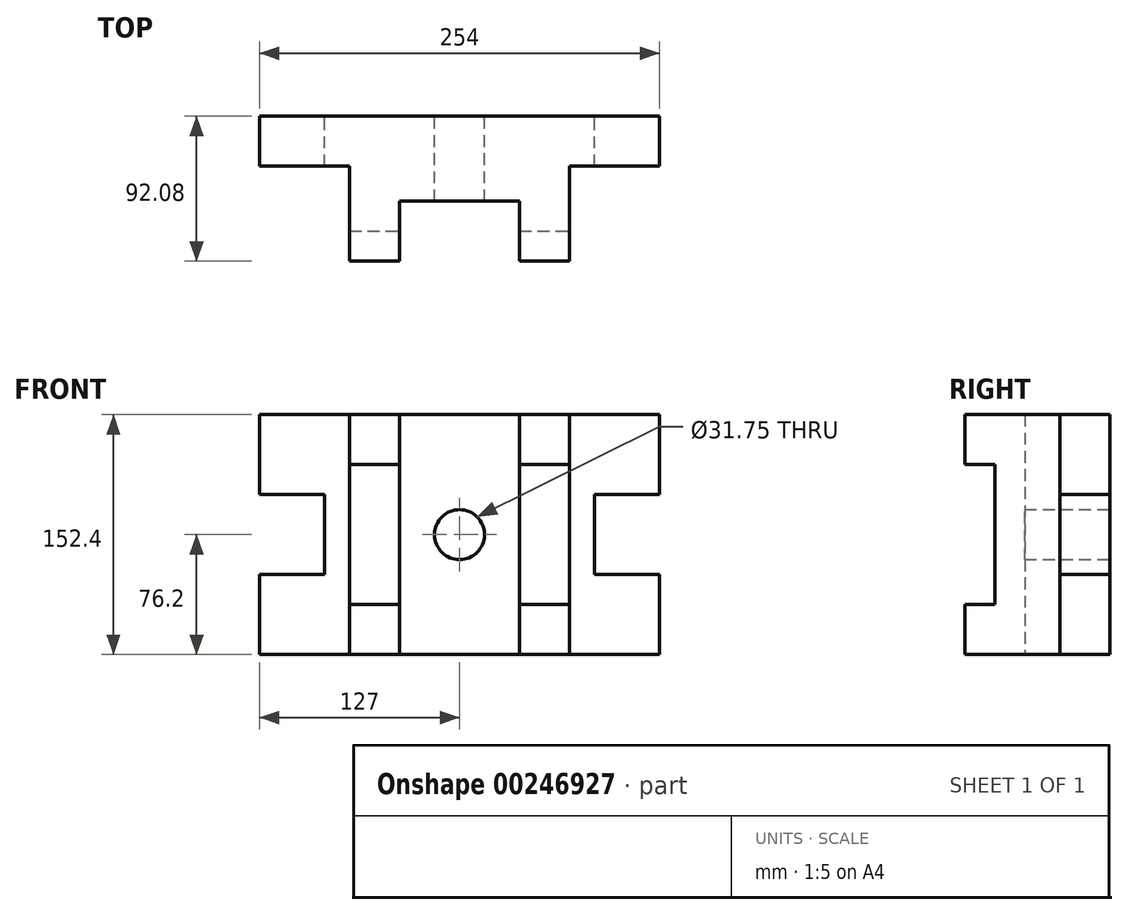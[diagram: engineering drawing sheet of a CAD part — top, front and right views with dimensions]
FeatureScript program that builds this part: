
annotation { "Feature Type Name" : "Feature", "Feature Type Description" : "" }
export const myFeature = defineFeature(function(context is Context, id is Id, definition is map)
    precondition{}
    {
        {
            var Q0;
            Q0=qCreatedBy(makeId("Front.planeOp"),FACE);
            var sketch = newSketch(context, id + "F0", { "sketchPlane" : qUnion([Q0])});
            skCircle(sketch, "E0", {"center": v(0, 0) * mm, "radius": 15.88 * mm});
            skLineSegment(sketch, "E1.bottom", {"start": v(-38.1, 76.2) * mm, "end": v(38.1, 76.2) * mm});
            skLineSegment(sketch, "E1.top", {"start": v(-38.1, -76.2) * mm, "end": v(38.1, -76.2) * mm});
            skLineSegment(sketch, "E1.left", {"start": v(-38.1, 76.2) * mm, "end": v(-38.1, -76.2) * mm});
            skLineSegment(sketch, "E1.right", {"start": v(38.1, 76.2) * mm, "end": v(38.1, -76.2) * mm});
            skLineSegment(sketch, "E2.bottom", {"start": v(-69.85, 76.2) * mm, "end": v(-38.1, 76.2) * mm});
            skLineSegment(sketch, "E2.top", {"start": v(-69.85, -76.2) * mm, "end": v(-38.1, -76.2) * mm});
            skLineSegment(sketch, "E2.left", {"start": v(-69.85, 76.2) * mm, "end": v(-69.85, -76.2) * mm});
            skPoint(sketch, "E2.middle", {"position": v(-53.97, 0) * mm});
            skLineSegment(sketch, "E3.top", {"start": v(98.71, -76.2) * mm, "end": v(130.46, -76.2) * mm});
            skLineSegment(sketch, "E4.bottom", {"start": v(69.85, 76.2) * mm, "end": v(127, 76.2) * mm});
            skLineSegment(sketch, "E4.top", {"start": v(69.85, -76.2) * mm, "end": v(127, -76.2) * mm});
            skLineSegment(sketch, "E4.left", {"start": v(69.85, 76.2) * mm, "end": v(69.85, -76.2) * mm});
            skLineSegment(sketch, "E4.right", {"start": v(127, 76.2) * mm, "end": v(127, -76.2) * mm});
            skPoint(sketch, "E4.middle", {"position": v(98.42, 0) * mm});
            skLineSegment(sketch, "E5.bottom", {"start": v(-69.85, 76.2) * mm, "end": v(-127, 76.2) * mm});
            skLineSegment(sketch, "E5.top", {"start": v(-69.85, -76.2) * mm, "end": v(-127, -76.2) * mm});
            skLineSegment(sketch, "E5.right", {"start": v(-127, 76.2) * mm, "end": v(-127, -76.2) * mm});
            skPoint(sketch, "E5.middle", {"position": v(-98.43, 0) * mm});
            skLineSegment(sketch, "E6", {"start": v(-69.85, 44.45) * mm, "end": v(-38.1, 44.45) * mm});
            skLineSegment(sketch, "E7", {"start": v(-69.85, -44.45) * mm, "end": v(-38.1, -44.45) * mm});
            skLineSegment(sketch, "E8.bottom", {"start": v(38.1, 76.2) * mm, "end": v(69.85, 76.2) * mm});
            skLineSegment(sketch, "E8.top", {"start": v(38.1, -76.2) * mm, "end": v(69.85, -76.2) * mm});
            skPoint(sketch, "E8.middle", {"position": v(53.98, 0) * mm});
            skLineSegment(sketch, "E9", {"start": v(38.1, 44.45) * mm, "end": v(69.85, 44.45) * mm});
            skLineSegment(sketch, "E10", {"start": v(38.1, -44.45) * mm, "end": v(69.85, -44.45) * mm});
            skLineSegment(sketch, "E11", {"start": v(-127, 25.4) * mm, "end": v(-85.72, 25.4) * mm});
            skLineSegment(sketch, "E12", {"start": v(-85.72, 25.4) * mm, "end": v(-85.72, -25.4) * mm});
            skLineSegment(sketch, "E13", {"start": v(-85.72, -25.4) * mm, "end": v(-127, -25.4) * mm});
            skLineSegment(sketch, "E14", {"start": v(127, 25.4) * mm, "end": v(85.72, 25.4) * mm});
            skLineSegment(sketch, "E15", {"start": v(85.72, 25.4) * mm, "end": v(85.72, -25.4) * mm});
            skLineSegment(sketch, "E16", {"start": v(85.72, -25.4) * mm, "end": v(127, -25.4) * mm});
            skSolve(sketch);
        }
        {
            var Q0;
            Q0=makeQuery(id+"F0.imprint","IMPRINT",FACE,{"disambiguationData":[TD([[makeQuery(id+"F0.imprint","IMPRINT",EDGE,{"derivedFrom":sQuery(id+"F0.wireOp",EDGE,"E0")}),-1.0]])]});
            extrude(context, id + "F1", {"entities" : qUnion([Q0]), "depth" : 53.97 * mm});
        }
        {
            var Q0;
            {var subQ0=sQuery(id+"F0.wireOp",EDGE,"E2.bottom");Q0=makeQuery(id+"F0.imprint","IMPRINT",FACE,{"disambiguationData":[TD([[makeQuery(id+"F0.imprint","IMPRINT",EDGE,{"derivedFrom":subQ0}),-1.0]])]});}
            var Q1;
            {var subQ0=sQuery(id+"F0.wireOp",EDGE,"E2.top");Q1=makeQuery(id+"F0.imprint","IMPRINT",FACE,{"disambiguationData":[TD([[makeQuery(id+"F0.imprint","IMPRINT",EDGE,{"derivedFrom":subQ0}),1.0]])]});}
            var Q2;
            {var subQ0=sQuery(id+"F0.wireOp",EDGE,"E8.top");Q2=makeQuery(id+"F0.imprint","IMPRINT",FACE,{"disambiguationData":[TD([[makeQuery(id+"F0.imprint","IMPRINT",EDGE,{"derivedFrom":subQ0}),1.0]])]});}
            var Q3;
            {var subQ0=sQuery(id+"F0.wireOp",EDGE,"E8.bottom");Q3=makeQuery(id+"F0.imprint","IMPRINT",FACE,{"disambiguationData":[TD([[makeQuery(id+"F0.imprint","IMPRINT",EDGE,{"derivedFrom":subQ0}),-1.0]])]});}
            extrude(context, id + "F2", {"entities" : qUnion([Q0, Q1, Q2, Q3]), "operationType" : NewBodyOperationType.ADD, "depth" : 92.07 * mm});
        }
        {
            var Q0;
            {var subQ0=sQuery(id+"F0.wireOp",EDGE,"E6");Q0=makeQuery(id+"F0.imprint","IMPRINT",FACE,{"disambiguationData":[TD([[makeQuery(id+"F0.imprint","IMPRINT",EDGE,{"derivedFrom":subQ0}),-1.0]])]});}
            var Q1;
            {var subQ0=sQuery(id+"F0.wireOp",EDGE,"E9");Q1=makeQuery(id+"F0.imprint","IMPRINT",FACE,{"disambiguationData":[TD([[makeQuery(id+"F0.imprint","IMPRINT",EDGE,{"derivedFrom":subQ0}),-1.0]])]});}
            extrude(context, id + "F3", {"entities" : qUnion([Q0, Q1]), "operationType" : NewBodyOperationType.ADD, "depth" : 73.02 * mm});
        }
        {
            var Q0;
            {var subQ3=sQuery(id+"F0.wireOp",EDGE,"E5.bottom");Q0=makeQuery(id+"F0.imprint","IMPRINT",FACE,{"disambiguationData":[TD([[makeQuery(id+"F0.imprint","IMPRINT",EDGE,{"derivedFrom":subQ3}),1.0]])]});}
            var Q1;
            {var subQ5=sQuery(id+"F0.wireOp",EDGE,"E4.bottom");Q1=makeQuery(id+"F0.imprint","IMPRINT",FACE,{"disambiguationData":[TD([[makeQuery(id+"F0.imprint","IMPRINT",EDGE,{"derivedFrom":subQ5}),-1.0]])]});}
            extrude(context, id + "F4", {"entities" : qUnion([Q0, Q1]), "operationType" : NewBodyOperationType.ADD, "depth" : 31.75 * mm});
        }
        {
            var Q0;
            Q0=makeQuery(id+"F0.imprint","IMPRINT",FACE,{"disambiguationData":[TD([[makeQuery(id+"F0.imprint","IMPRINT",EDGE,{"derivedFrom":sQuery(id+"F0.wireOp",EDGE,"E0")}),1.0]])]});
            var Q1;
            {var subQ0=sQuery(id+"F0.wireOp",EDGE,"E11");Q1=makeQuery(id+"F0.imprint","IMPRINT",FACE,{"disambiguationData":[TD([[makeQuery(id+"F0.imprint","IMPRINT",EDGE,{"derivedFrom":subQ0}),-1.0]])]});}
            var Q2;
            {var subQ0=sQuery(id+"F0.wireOp",EDGE,"E14");Q2=makeQuery(id+"F0.imprint","IMPRINT",FACE,{"disambiguationData":[TD([[makeQuery(id+"F0.imprint","IMPRINT",EDGE,{"derivedFrom":subQ0}),1.0]])]});}
            extrude(context, id + "F5", {"entities" : qUnion([Q0, Q1, Q2]), "operationType" : NewBodyOperationType.REMOVE, "endBound" : BoundingType.THROUGH_ALL, "oppositeDirection" : true, "depth" : 25.4 * mm});
        }
    });
